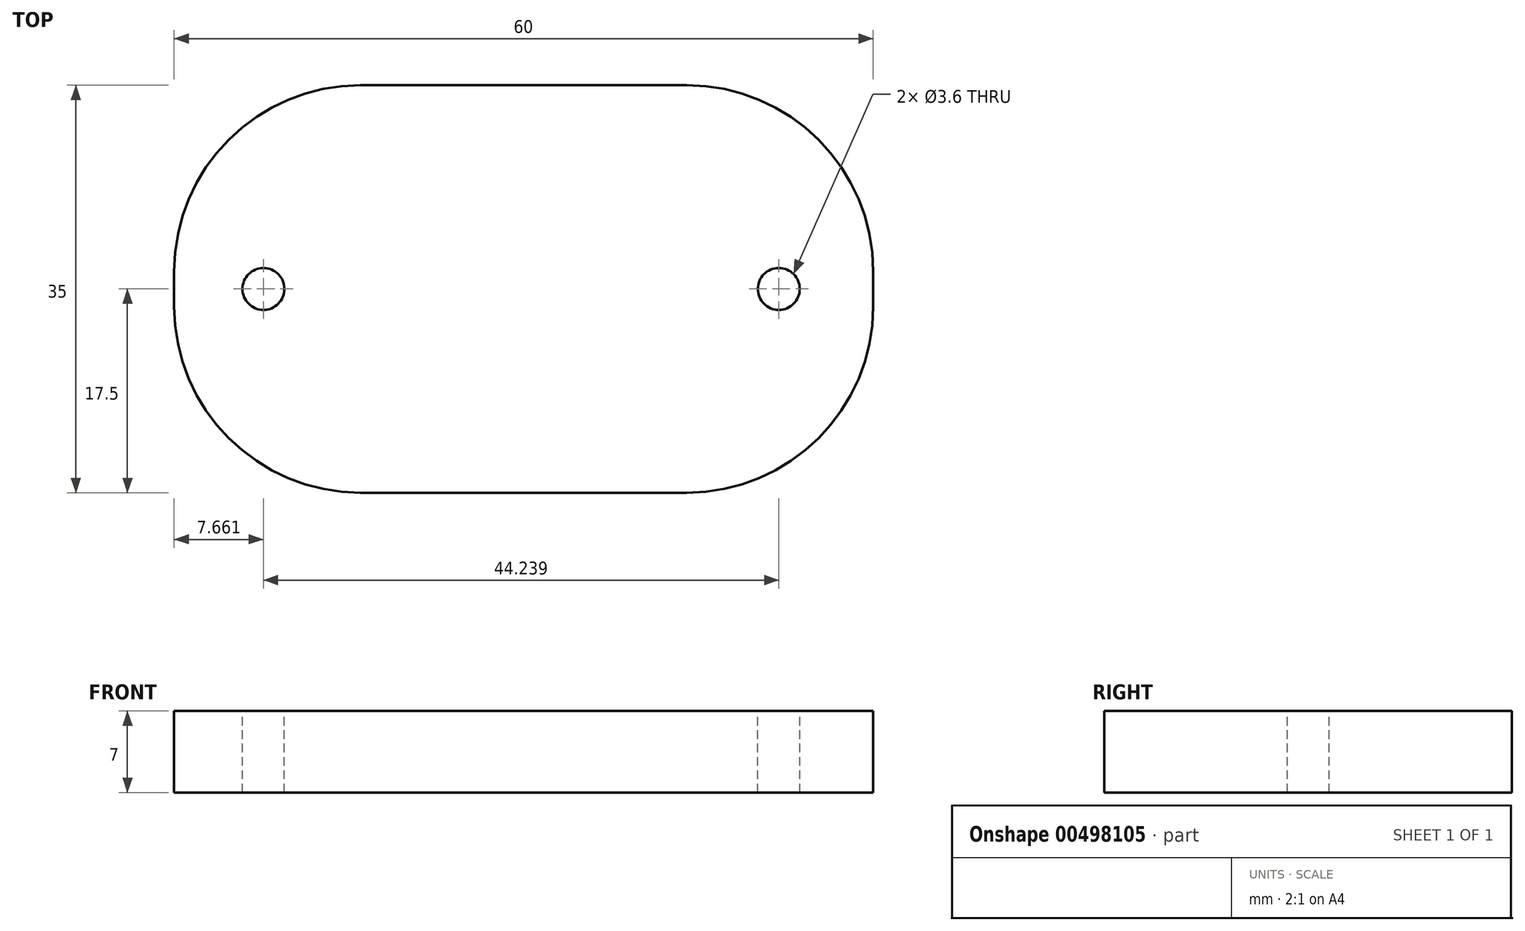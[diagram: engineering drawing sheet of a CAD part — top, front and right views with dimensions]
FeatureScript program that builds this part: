
annotation { "Feature Type Name" : "Feature", "Feature Type Description" : "" }
export const myFeature = defineFeature(function(context is Context, id is Id, definition is map)
    precondition{}
    {
        {
            var Q0;
            Q0=qCreatedBy(makeId("Top.planeOp"),FACE);
            var sketch = newSketch(context, id + "F0", { "sketchPlane" : qUnion([Q0])});
            skLineSegment(sketch, "E0.bottom", {"start": v(14, 17.5) * mm, "end": v(-14, 17.5) * mm});
            skLineSegment(sketch, "E0.top", {"start": v(14, -17.5) * mm, "end": v(-14, -17.5) * mm});
            skLineSegment(sketch, "E0.left", {"start": v(30, 1.5) * mm, "end": v(30, -1.5) * mm});
            skLineSegment(sketch, "E0.right", {"start": v(-30, 1.5) * mm, "end": v(-30, -1.5) * mm});
            skPoint(sketch, "E0.middle", {"position": v(0, 0) * mm});
            skPoint(sketch, "E1.visualSharp", {"position": v(-30, 17.5) * mm});
            skArc(sketch, "E1.filletArc", {"start": v(-14, 17.5) * mm, "mid": v(-25.31, 12.81) * mm, "end": v(-30, 1.5) * mm});
            skPoint(sketch, "E2.visualSharp", {"position": v(-30, -17.5) * mm});
            skArc(sketch, "E2.filletArc", {"start": v(-30, -1.5) * mm, "mid": v(-25.31, -12.81) * mm, "end": v(-14, -17.5) * mm});
            skPoint(sketch, "E3.visualSharp", {"position": v(30, 17.5) * mm});
            skArc(sketch, "E3.filletArc", {"start": v(30, 1.5) * mm, "mid": v(25.31, 12.81) * mm, "end": v(14, 17.5) * mm});
            skPoint(sketch, "E4.visualSharp", {"position": v(30, -17.5) * mm});
            skArc(sketch, "E4.filletArc", {"start": v(14, -17.5) * mm, "mid": v(25.31, -12.81) * mm, "end": v(30, -1.5) * mm});
            skSolve(sketch);
        }
        {
            var Q0;
            Q0 = qSketchRegion(id + "F0", true);
            extrude(context, id + "F1", {"entities" : qUnion([Q0]), "endBound" : BoundingType.SYMMETRIC, "depth" : 7 * mm});
        }
        {
            var Q0;
            Q0=makeQuery(id+"F1.opExtrude","CAP_FACE",FACE,{"disambiguationData":[OSD([sQuery(id+"F0.wireOp",EDGE,"E0.bottom"),sQuery(id+"F0.wireOp",EDGE,"E0.top"),sQuery(id+"F0.wireOp",EDGE,"E0.left"),sQuery(id+"F0.wireOp",EDGE,"E0.right")])],"isStart":false});
            var sketch = newSketch(context, id + "F2", { "sketchPlane" : qUnion([Q0])});
            skCircle(sketch, "E5", {"center": v(-22.34, 0) * mm, "radius": 1.8 * mm});
            skPoint(sketch, "E5.centerSnap0", {"position": v(-30, 0) * mm});
            skSolve(sketch);
        }
        {
            var Q0;
            Q0 = qSketchRegion(id + "F2", true);
            extrude(context, id + "F3", {"entities" : qUnion([Q0]), "operationType" : NewBodyOperationType.REMOVE, "oppositeDirection" : true, "depth" : 8 * mm});
        }
        {
            var Q0;
            Q0=makeQuery(id+"F1.opExtrude","CAP_FACE",FACE,{"disambiguationData":[OSD([sQuery(id+"F0.wireOp",EDGE,"E0.bottom"),sQuery(id+"F0.wireOp",EDGE,"E0.top"),sQuery(id+"F0.wireOp",EDGE,"E0.left"),sQuery(id+"F0.wireOp",EDGE,"E0.right")])],"isStart":false});
            var sketch = newSketch(context, id + "F4", { "sketchPlane" : qUnion([Q0])});
            skCircle(sketch, "E6", {"center": v(21.9, 0) * mm, "radius": 1.8 * mm});
            skPoint(sketch, "E6.centerSnap0", {"position": v(30, 0) * mm});
            skSolve(sketch);
        }
        {
            var Q0;
            Q0 = qSketchRegion(id + "F4", true);
            extrude(context, id + "F5", {"entities" : qUnion([Q0]), "operationType" : NewBodyOperationType.REMOVE, "oppositeDirection" : true, "depth" : 8 * mm});
        }
    });
